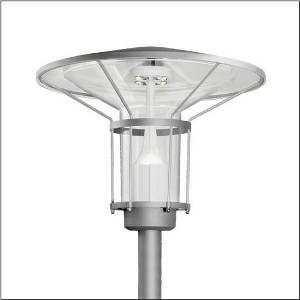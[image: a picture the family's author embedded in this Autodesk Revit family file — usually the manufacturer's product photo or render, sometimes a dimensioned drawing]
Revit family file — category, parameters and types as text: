
# Revit family: laterne_classic_iq___st1_2a_5xa5245kf14h_95b8
name_source: partatom
category: Lighting Fixtures
units: mm (PartAtom-declared; Revit-internal decimal feet)

## family parameters
Cut with Voids When Loaded = No
Host = Face
Light Source = No
Part Type = Normal
Room Calculation Point = No
Round Connector Dimension = Use Diameter
Shared = No

## types (1)
- --- (1 x LED, 1380 lm, 10 W, 4000K)
    Apparent Load = 10 VA
    CIE Flux Codes = 21 60 93 97 100
    Color Rendering = 70
    Color Temperature = 4000K
    Default Elevation = 1800 mm
    Description = Lantern Classic iQ, mast luminaire, Module 540 iQ-SR, primary light control with 3 zone facetted reflector, of plastic, silver coated, highly specular, structured, primary optical cover: cover, of PMMA, transparent, light distribution: ST1.2a, light emission: direct distribution, primary light characteristic: asymmetric, installation type: post-top, LED, High Power LED, rated luminous flux: 1.380lm, luminous efficacy: 138lm/W, light colour: 740, colour temperature: 4000K, control gear: iQ Street-Remote, control: pre-setting: logarithmic dimming characteristic, Street-Remote, Auto-Match, Temp-Guard, Lumen-Switch, Night-Set, Smart-Wire, Light-Fading, Desk-Remote (wireless, voltage-free reading and setting of iQ features in the workshop via application-optimized NFC function/RFID function), optimised constant luminous flux control (CLO 2.0), with terminal, 6-pole, max. 2.5mm², mains connection: 230..240V, AC, 50/60Hz, start of lifetime: 10W, end of service life: 10W, reduction: 5W, luminaire housing, upper part, of glass-fibre reinforced polyester, coated, Siteco® metallic grey (DB 702S), diameter: 750mm, height: 596mm, spigot size: d x l = 76 x 70mm (post-top) | with reducer (optional accessory) 60 x 70mm, mounting height: 3..5m, post-top mast mounting element, of diecast aluminium, coated, Siteco® metallic grey (DB 702S), Module 540 iQ-SR, traffic white (RAL 9016), equipment: standard, protection rating (complete): IP65, insulation class (complete): insulation class II (safety insulation), certification: CE, ENEC, VDE, packaging unit: 1 piece

Light Distribution: ST1.2a
    Height = 596 mm
    Lamp = 1 x LED
    Lamp Light Flux = 1380 lm
    Lamp Power = 10 W
    Lamp count = 1
    Length = 750 mm
    Luminous efficacy = 138 lm/W
    Manufacturer = Siteco
    ModVariant = No
    Model = 5XA5245KF14H
    Number of Poles = 1
    OnlyDefault = Yes
    Power Factor = 1
    Product Name = Laterne Classic iQ | ST1.2a
    Product group = mast luminaire | pylon top
    ProductGroupID = 6100
    Protection Class = Protection class II
    Protection Degree = IP 65
    RLX_Detail_Level = 1
    RLX_Emergency_Light_Flux = 0 lm
    RLX_Emergency_Type = 0
    RLX_Emergency_Type_DB = No
    RlxData = <blob elided: 70849 chars, md5=ea3a24af>
    Socket = socket
    Standby Power = 0 W
    System Light Flux = 1380 lm
    System Power = 10 W
    Type Comments = factory setting: luminous flux: 100 % | dim-lin: 254 | 401 mA
    Type Image = l_1006052.jpg
    URL = http://relux.com
    VarID = @adj_160368
    Voltage = 0 V
    Weight = 0.00 kg
    Width = 0 mm  [stored 0 ft]

note: [stored X ft] marks values corroborated as IEEE doubles in the binary element streams (Revit-internal decimal feet)

## geometry (parser evidence)
native form markers: Blend x4, Sweep x11
no freeform markers — native parametric forms only
